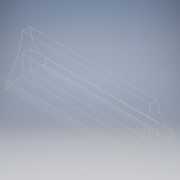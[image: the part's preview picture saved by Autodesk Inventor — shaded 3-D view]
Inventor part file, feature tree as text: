
AUTODESK INVENTOR PART (.ipt)
format: ipt  version: 2022.2 (Build 262287010, 287A)  size: 312,320 bytes
history: native  units: in
note: dims shown in document units (in); Inventor stores cm internally (conversion verified against a paired STEP export)
features: other x1, direct_edit x1, revolve x1
ambient origin geometry x8: Origin, YZ Plane, XZ Plane, XY Plane, X Axis, Y Axis, Z Axis, Center Point
bodies: Solid1 (feature_tree)
feature tree (3):
  other  "North (8)"
  direct_edit  "Direct Edit1"
  revolve  "Rotate1"  [1 undecoded]
note: 1 required parameter value undecoded (feature->parameter linkage not recoverable at this tier; creation-order binding heuristic only, values carry confidence <= 0.55)
